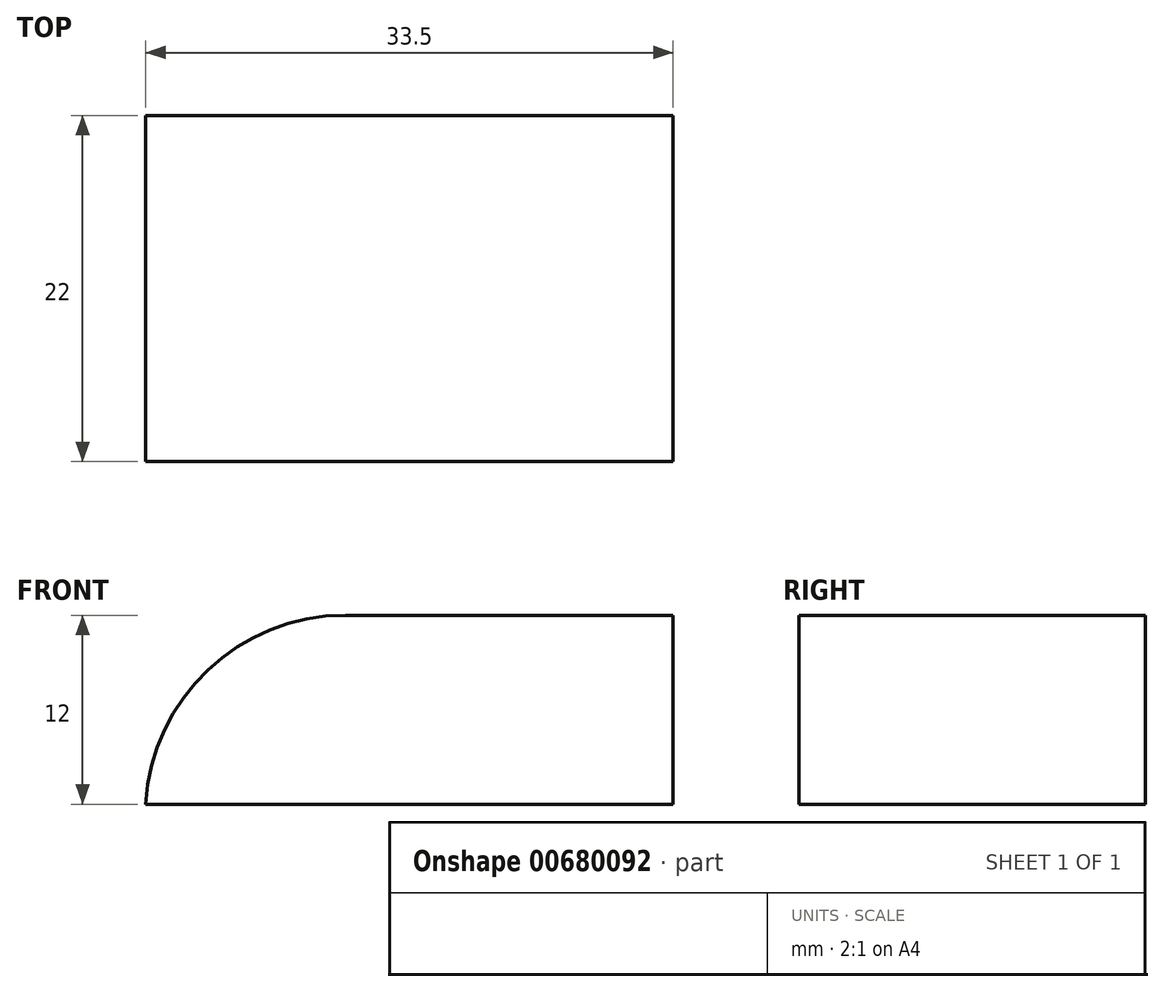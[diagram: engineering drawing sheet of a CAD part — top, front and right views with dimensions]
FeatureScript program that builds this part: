
annotation { "Feature Type Name" : "Feature", "Feature Type Description" : "" }
export const myFeature = defineFeature(function(context is Context, id is Id, definition is map)
    precondition{}
    {
        {
            var Q0;
            Q0=qCreatedBy(makeId("Top.planeOp"),FACE);
            var sketch = newSketch(context, id + "F0", { "sketchPlane" : qUnion([Q0])});
            skLineSegment(sketch, "E0.bottom", {"start": v(16.75, 11) * mm, "end": v(-16.75, 11) * mm});
            skLineSegment(sketch, "E0.top", {"start": v(16.75, -11) * mm, "end": v(-16.75, -11) * mm});
            skLineSegment(sketch, "E0.left", {"start": v(16.75, 11) * mm, "end": v(16.75, -11) * mm});
            skLineSegment(sketch, "E0.right", {"start": v(-16.75, 11) * mm, "end": v(-16.75, -11) * mm});
            skPoint(sketch, "E0.middle", {"position": v(0, 0) * mm});
            skSolve(sketch);
        }
        {
            var Q0;
            Q0 = qSketchRegion(id + "F0", true);
            extrude(context, id + "F1", {"entities" : qUnion([Q0]), "depth" : 12 * mm, "offsetDistance" : 25.4 * mm});
        }
        {
            var Q0;
            Q0=makeQuery(id+"F1.opExtrude","CAP_EDGE",EDGE,{"disambiguationData":[OSD([sQuery(id+"F0.wireOp",EDGE,"E0.right")])],"isStart":false});
            fillet(context, id + "F2", {"entities" : qUnion([Q0]), "radius" : 12.7 * mm, "tangentPropagation" : true, "allowEdgeOverflow" : false});
        }
    });
